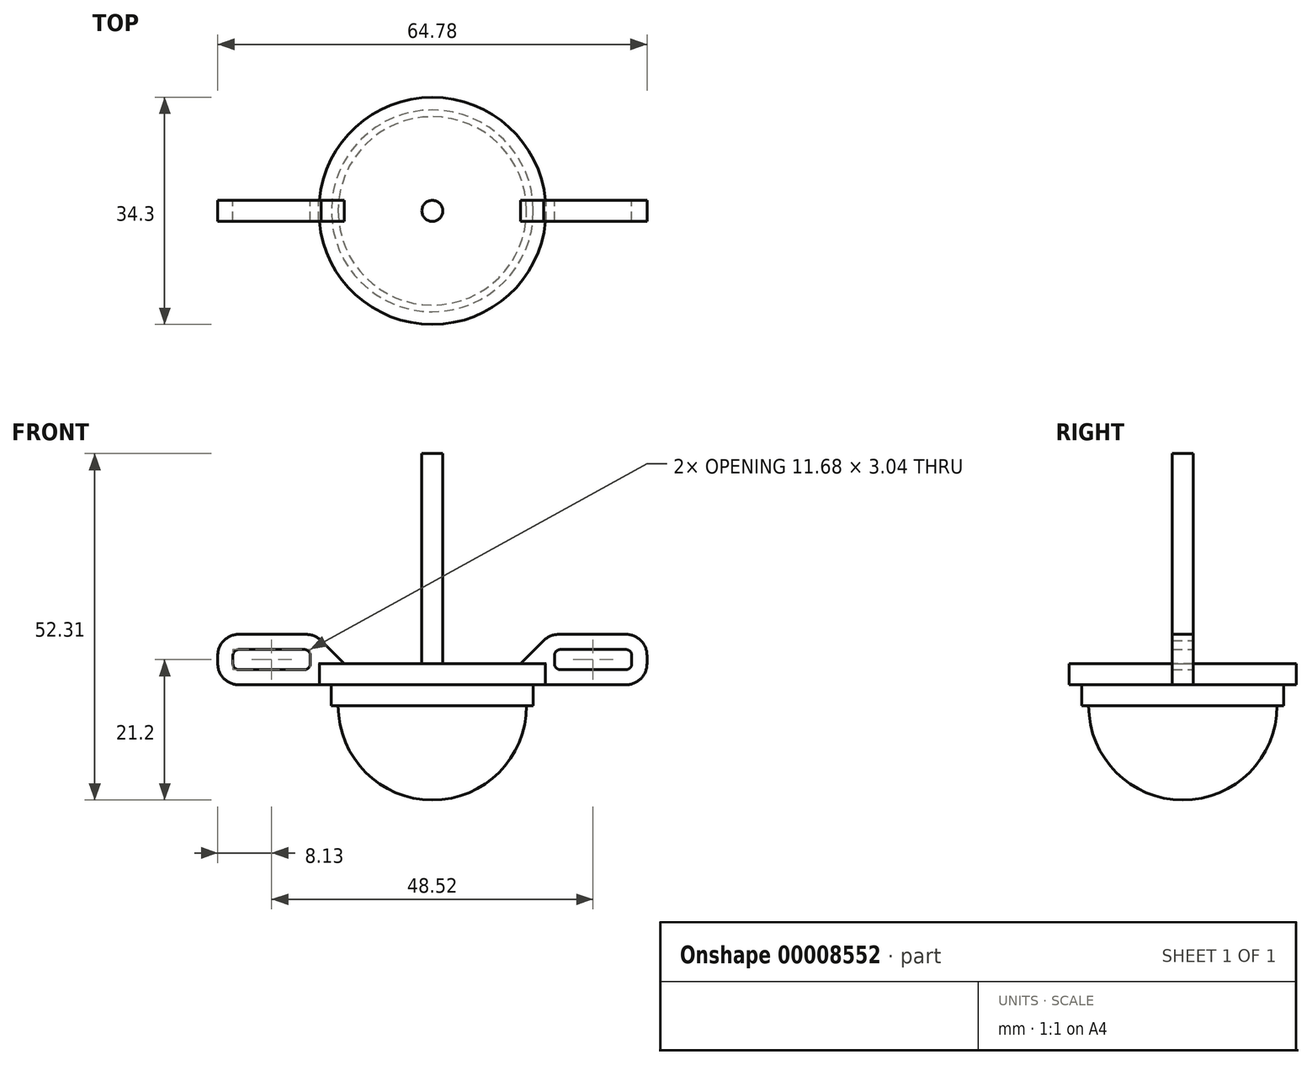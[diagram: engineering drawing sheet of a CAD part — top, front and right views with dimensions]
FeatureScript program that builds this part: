
annotation { "Feature Type Name" : "Feature", "Feature Type Description" : "" }
export const myFeature = defineFeature(function(context is Context, id is Id, definition is map)
    precondition{}
    {
        {
            var Q0;
            Q0=qCreatedBy(makeId("Top.planeOp"),FACE);
            var sketch = newSketch(context, id + "F0", { "sketchPlane" : qUnion([Q0])});
            skCircle(sketch, "E0", {"center": v(0, 0) * mm, "radius": 17.15 * mm});
            skSolve(sketch);
        }
        {
            var Q0;
            Q0 = qSketchRegion(id + "F0", true);
            extrude(context, id + "F1", {"entities" : qUnion([Q0]), "depth" : 3.17 * mm});
        }
        {
            var Q0;
            Q0=makeQuery(id+"F1.opExtrude","CAP_FACE",FACE,{"disambiguationData":[OSD([sQuery(id+"F0.wireOp",EDGE,"E0")])],"isStart":false});
            var sketch = newSketch(context, id + "F2", { "sketchPlane" : qUnion([Q0])});
            skPoint(sketch, "E1.1", {"position": v(0, 0) * mm});
            skCircle(sketch, "E2", {"center": v(9.53, 0) * mm, "radius": 1.59 * mm});
            skCircle(sketch, "E3", {"center": v(-9.53, 0) * mm, "radius": 1.59 * mm});
            skLineSegment(sketch, "E4", {"start": v(-9.53, 0) * mm, "end": v(9.53, 0) * mm, "construction": true});
            skCircle(sketch, "E5", {"center": v(0, 0) * mm, "radius": 1.59 * mm});
            skCircle(sketch, "E6.1.0", {"center": v(0, 9.53) * mm, "radius": 1.59 * mm});
            skCircle(sketch, "E6.3.0", {"center": v(0, -9.53) * mm, "radius": 1.59 * mm});
            skSolve(sketch);
        }
        {
            var Q0;
            Q0=makeQuery(id+"F2.imprint","IMPRINT",FACE,{"disambiguationData":[TD([[makeQuery(id+"F2.imprint","IMPRINT",EDGE,{"derivedFrom":sQuery(id+"F2.wireOp",EDGE,"E5")}),1.0]])]});
            extrude(context, id + "F3", {"entities" : qUnion([Q0]), "operationType" : NewBodyOperationType.ADD, "depth" : 31.75 * mm});
        }
        {
            var Q0;
            Q0=makeQuery(id+"F1.opExtrude","CAP_FACE",FACE,{"disambiguationData":[OSD([sQuery(id+"F0.wireOp",EDGE,"E0")])],"isStart":true});
            var sketch = newSketch(context, id + "F4", { "sketchPlane" : qUnion([Q0])});
            skCircle(sketch, "E7", {"center": v(0, 0) * mm, "radius": 15.24 * mm});
            skSolve(sketch);
        }
        {
            var Q0;
            Q0=makeQuery(id+"F4.imprint","IMPRINT",FACE,{"disambiguationData":[TD([[makeQuery(id+"F4.imprint","IMPRINT",EDGE,{"derivedFrom":sQuery(id+"F4.wireOp",EDGE,"E7")}),1.0]])]});
            extrude(context, id + "F5", {"entities" : qUnion([Q0]), "operationType" : NewBodyOperationType.ADD, "depth" : 3.17 * mm});
        }
        {
            var Q0;
            Q0=qCreatedBy(makeId("Front.planeOp"),FACE);
            var sketch = newSketch(context, id + "F6", { "sketchPlane" : qUnion([Q0])});
            skLineSegment(sketch, "E8.1", {"start": v(-17.15, 3.18) * mm, "end": v(17.15, 3.18) * mm});
            skLineSegment(sketch, "E9.3", {"start": v(-17.15, 0) * mm, "end": v(17.15, 0) * mm});
            skLineSegment(sketch, "E10", {"start": v(17.15, 3.18) * mm, "end": v(17.15, 0) * mm});
            skLineSegment(sketch, "E11", {"start": v(17.15, 0) * mm, "end": v(29.21, 0) * mm});
            skLineSegment(sketch, "E12", {"start": v(32.39, 3.18) * mm, "end": v(32.39, 4.45) * mm});
            skLineSegment(sketch, "E13", {"start": v(29.21, 7.62) * mm, "end": v(19.05, 7.62) * mm});
            skLineSegment(sketch, "E14", {"start": v(16.8, 6.7) * mm, "end": v(13.29, 3.17) * mm});
            skLineSegment(sketch, "E15", {"start": v(17.15, 3.18) * mm, "end": v(17.15, 7.03) * mm});
            skPoint(sketch, "E16.visualSharp", {"position": v(32.39, 7.62) * mm});
            skArc(sketch, "E16.filletArc", {"start": v(32.39, 4.45) * mm, "mid": v(31.46, 6.7) * mm, "end": v(29.21, 7.62) * mm});
            skPoint(sketch, "E17.visualSharp", {"position": v(32.39, 0) * mm});
            skArc(sketch, "E17.filletArc", {"start": v(29.21, 0) * mm, "mid": v(31.46, 0.93) * mm, "end": v(32.39, 3.18) * mm});
            skPoint(sketch, "E18.visualSharp", {"position": v(17.73, 7.62) * mm});
            skArc(sketch, "E18.filletArc", {"start": v(19.05, 7.62) * mm, "mid": v(17.83, 7.38) * mm, "end": v(16.8, 6.7) * mm});
            skLineSegment(sketch, "E19.0", {"start": v(29.21, 5.33) * mm, "end": v(21.21, 5.33) * mm});
            skArc(sketch, "E19.1", {"start": v(30.1, 4.45) * mm, "mid": v(29.84, 5.07) * mm, "end": v(29.21, 5.33) * mm});
            skLineSegment(sketch, "E19.2", {"start": v(30.1, 3.18) * mm, "end": v(30.1, 4.45) * mm});
            skArc(sketch, "E19.3", {"start": v(29.21, 2.29) * mm, "mid": v(29.84, 2.55) * mm, "end": v(30.1, 3.18) * mm});
            skLineSegment(sketch, "E19.4", {"start": v(19.3, 2.29) * mm, "end": v(29.21, 2.29) * mm});
            skLineSegment(sketch, "E20", {"start": v(21.21, 5.33) * mm, "end": v(19.3, 5.33) * mm});
            skLineSegment(sketch, "E21", {"start": v(18.42, 4.44) * mm, "end": v(18.42, 3.18) * mm});
            skPoint(sketch, "E22.visualSharp", {"position": v(18.42, 5.33) * mm});
            skArc(sketch, "E22.filletArc", {"start": v(19.3, 5.33) * mm, "mid": v(18.68, 5.07) * mm, "end": v(18.42, 4.44) * mm});
            skPoint(sketch, "E23.visualSharp", {"position": v(18.42, 2.29) * mm});
            skArc(sketch, "E23.filletArc", {"start": v(18.42, 3.18) * mm, "mid": v(18.68, 2.55) * mm, "end": v(19.3, 2.29) * mm});
            skLineSegment(sketch, "E24.bottom", {"start": v(13.29, 3.17) * mm, "end": v(17.15, 3.17) * mm});
            skLineSegment(sketch, "E24.top", {"start": v(13.29, 0) * mm, "end": v(17.15, 0) * mm});
            skLineSegment(sketch, "E24.left", {"start": v(13.29, 3.18) * mm, "end": v(13.29, 0) * mm});
            skLineSegment(sketch, "E24.right", {"start": v(17.15, 3.17) * mm, "end": v(17.15, 0) * mm});
            skSolve(sketch);
        }
        {
            var Q0;
            Q0=makeQuery(id+"F6.imprint","IMPRINT",FACE,{"disambiguationData":[TD([[makeQuery(id+"F6.imprint","IMPRINT",EDGE,{"derivedFrom":sQuery(id+"F6.wireOp",EDGE,"E24.bottom")}),-1.0]])]});
            var Q1;
            {var subQ1=sQuery(id+"F6.wireOp",EDGE,"E15");Q1=makeQuery(id+"F6.imprint","IMPRINT",FACE,{"disambiguationData":[TD([[makeQuery(id+"F6.imprint","IMPRINT",EDGE,{"derivedFrom":subQ1}),1.0]])]});}
            var Q2;
            Q2=makeQuery(id+"F6.imprint","IMPRINT",FACE,{"disambiguationData":[TD([[makeQuery(id+"F6.imprint","IMPRINT",EDGE,{"derivedFrom":sQuery(id+"F6.wireOp",EDGE,"E11")}),1.0]])]});
            extrude(context, id + "F7", {"entities" : qUnion([Q0, Q1, Q2]), "operationType" : NewBodyOperationType.ADD, "endBound" : BoundingType.SYMMETRIC, "depth" : 3.17 * mm});
        }
        {
            var Q0;
            Q0=makeQuery(id+"F1.opExtrude","SWEPT_BODY",BODY,{"disambiguationData":[OSD([sQuery(id+"F0.wireOp",EDGE,"E0")])]});
            var Q1;
            Q1=qCreatedBy(makeId("Right.planeOp"),FACE);
            mirror(context, id + "F8", {"entities" : qUnion([Q0]), "mirrorPlane" : qUnion([Q1])});
        }
        {
            var Q0;
            Q0=makeQuery(id+"F5.opExtrude","CAP_FACE",FACE,{"disambiguationData":[OSD([sQuery(id+"F4.wireOp",EDGE,"E7")])],"isStart":false});
            var sketch = newSketch(context, id + "F9", { "sketchPlane" : qUnion([Q0])});
            skCircle(sketch, "E25.0.0", {"center": v(0, 0) * mm, "radius": 15.24 * mm});
            skCircle(sketch, "E26", {"center": v(0, 0) * mm, "radius": 14.22 * mm});
            skLineSegment(sketch, "E27", {"start": v(-14.22, 0) * mm, "end": v(14.22, 0) * mm});
            skSolve(sketch);
        }
        {
            var Q0;
            {var subQ0=sQuery(id+"F9.wireOp",EDGE,"E27");Q0=makeQuery(id+"F9.imprint","IMPRINT",FACE,{"disambiguationData":[TD([[makeQuery(id+"F9.imprint","IMPRINT",EDGE,{"derivedFrom":subQ0}),1.0]])]});}
            var Q1;
            Q1=sQuery(id+"F9.wireOp",EDGE,"E27");
            revolve(context, id + "F10", {"operationType" : NewBodyOperationType.ADD, "entities" : qUnion([Q0]), "axis" : qUnion([Q1]), "revolveType" : RevolveType.ONE_DIRECTION, "angle" : 180 * degree});
        }
    });
